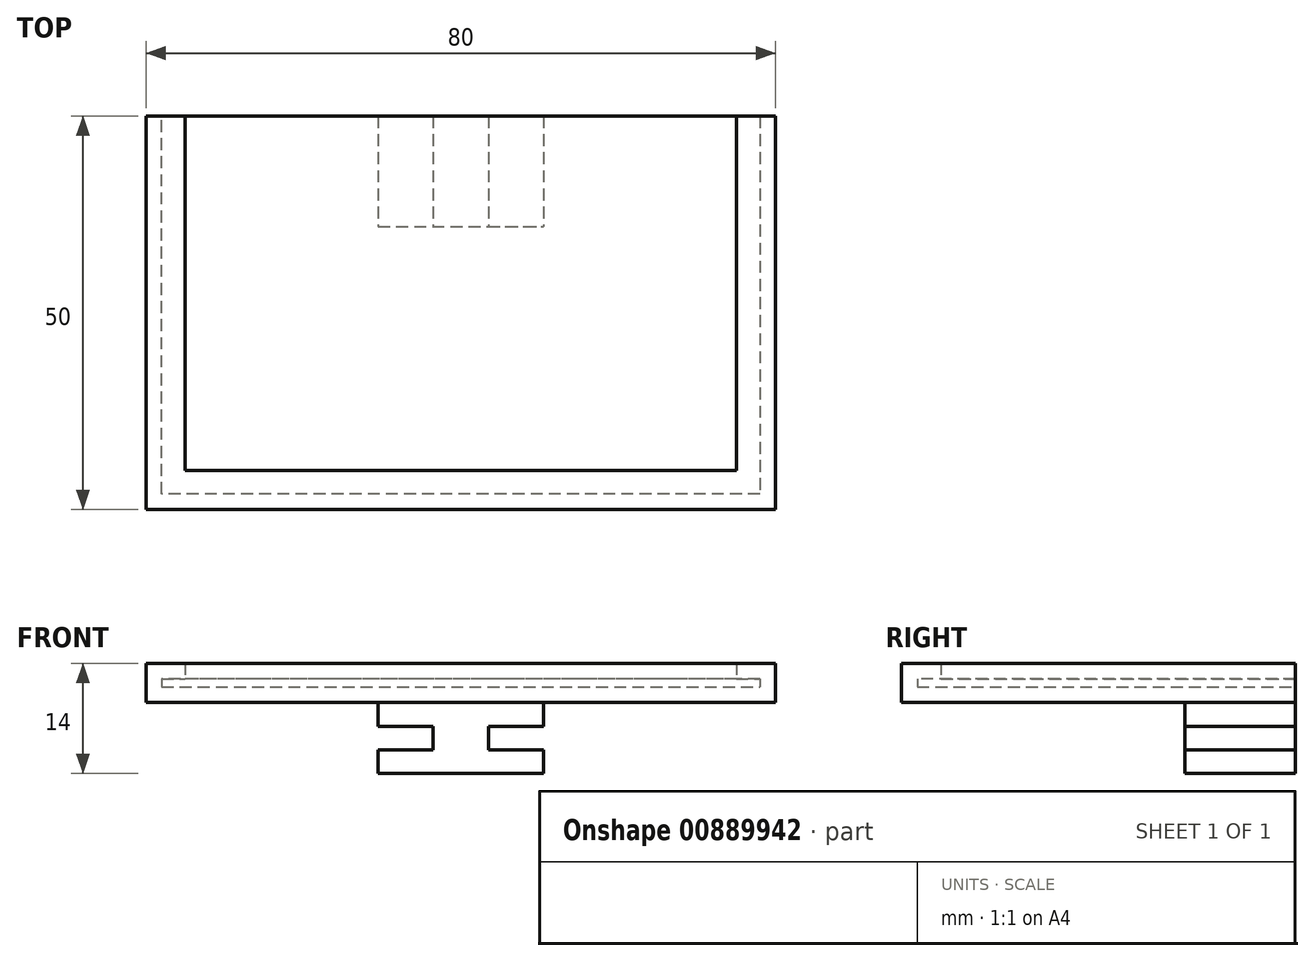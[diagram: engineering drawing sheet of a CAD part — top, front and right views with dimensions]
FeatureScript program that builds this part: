
annotation { "Feature Type Name" : "Feature", "Feature Type Description" : "" }
export const myFeature = defineFeature(function(context is Context, id is Id, definition is map)
    precondition{}
    {
        {
            var Q0;
            Q0=qCreatedBy(makeId("Top.planeOp"),FACE);
            var sketch = newSketch(context, id + "F0", { "sketchPlane" : qUnion([Q0])});
            skLineSegment(sketch, "E0.bottom", {"start": v(-10.5, 7) * mm, "end": v(10.5, 7) * mm});
            skLineSegment(sketch, "E0.top", {"start": v(-10.5, -7) * mm, "end": v(10.5, -7) * mm});
            skLineSegment(sketch, "E0.left", {"start": v(-10.5, 7) * mm, "end": v(-10.5, -7) * mm});
            skLineSegment(sketch, "E0.right", {"start": v(10.5, 7) * mm, "end": v(10.5, -7) * mm});
            skSolve(sketch);
        }
        {
            var Q0;
            Q0=makeQuery(id+"F0.imprint","IMPRINT",FACE,{"disambiguationData":[TD([[makeQuery(id+"F0.imprint","IMPRINT",EDGE,{"derivedFrom":sQuery(id+"F0.wireOp",EDGE,"E0.bottom")}),-1.0]])]});
            extrude(context, id + "F1", {"entities" : qUnion([Q0]), "depth" : 3 * mm, "offsetDistance" : 25 * mm});
        }
        {
            var Q0;
            Q0=makeQuery(id+"F1.opExtrude","CAP_FACE",FACE,{"disambiguationData":[OSD([sQuery(id+"F0.wireOp",EDGE,"E0.bottom"),sQuery(id+"F0.wireOp",EDGE,"E0.top"),sQuery(id+"F0.wireOp",EDGE,"E0.left"),sQuery(id+"F0.wireOp",EDGE,"E0.right")])],"isStart":false});
            var sketch = newSketch(context, id + "F2", { "sketchPlane" : qUnion([Q0])});
            skLineSegment(sketch, "E1.bottom", {"start": v(-3.5, 7) * mm, "end": v(3.5, 7) * mm});
            skLineSegment(sketch, "E1.top", {"start": v(-3.5, -7) * mm, "end": v(3.5, -7) * mm});
            skLineSegment(sketch, "E1.left", {"start": v(-3.5, 7) * mm, "end": v(-3.5, -7) * mm});
            skLineSegment(sketch, "E1.right", {"start": v(3.5, 7) * mm, "end": v(3.5, -7) * mm});
            skSolve(sketch);
        }
        {
            var Q0;
            Q0=makeQuery(id+"F2.imprint","IMPRINT",FACE,{"disambiguationData":[TD([[makeQuery(id+"F2.imprint","IMPRINT",EDGE,{"derivedFrom":sQuery(id+"F2.wireOp",EDGE,"E1.bottom")}),-1.0]])]});
            extrude(context, id + "F3", {"entities" : qUnion([Q0]), "operationType" : NewBodyOperationType.ADD, "depth" : 1.5 * mm, "offsetDistance" : 25 * mm});
        }
        {
            var Q0;
            Q0=makeQuery(id+"F1.opExtrude","SWEPT_BODY",BODY,{"disambiguationData":[OSD([sQuery(id+"F0.wireOp",EDGE,"E0.bottom"),sQuery(id+"F0.wireOp",EDGE,"E0.top"),sQuery(id+"F0.wireOp",EDGE,"E0.left"),sQuery(id+"F0.wireOp",EDGE,"E0.right")])]});
            var Q1;
            Q1=makeQuery(id+"F3.opExtrude","CAP_FACE",FACE,{"disambiguationData":[OSD([sQuery(id+"F2.wireOp",EDGE,"E1.bottom"),sQuery(id+"F2.wireOp",EDGE,"E1.top"),sQuery(id+"F2.wireOp",EDGE,"E1.left"),sQuery(id+"F2.wireOp",EDGE,"E1.right")])],"isStart":false});
            mirror(context, id + "F4", {"operationType" : NewBodyOperationType.ADD, "entities" : qUnion([Q0]), "mirrorPlane" : qUnion([Q1])});
        }
        {
            var Q0;
            Q0=makeQuery(id+"F4.opPattern","COPY",FACE,{"derivedFrom":makeQuery(id+"F1.opExtrude","CAP_FACE",FACE,{"disambiguationData":[OSD([sQuery(id+"F0.wireOp",EDGE,"E0.bottom"),sQuery(id+"F0.wireOp",EDGE,"E0.top"),sQuery(id+"F0.wireOp",EDGE,"E0.left"),sQuery(id+"F0.wireOp",EDGE,"E0.right")])],"isStart":true}),"instanceName":"1"});
            var sketch = newSketch(context, id + "F5", { "sketchPlane" : qUnion([Q0])});
            skLineSegment(sketch, "E2.bottom", {"start": v(-40, 7) * mm, "end": v(40, 7) * mm});
            skLineSegment(sketch, "E2.top", {"start": v(-40, -43) * mm, "end": v(40, -43) * mm});
            skLineSegment(sketch, "E2.left", {"start": v(-40, 7) * mm, "end": v(-40, -43) * mm});
            skLineSegment(sketch, "E2.right", {"start": v(40, 7) * mm, "end": v(40, -43) * mm});
            skSolve(sketch);
        }
        {
            var Q0;
            Q0 = qSketchRegion(id + "F5", true);
            extrude(context, id + "F6", {"entities" : qUnion([Q0]), "operationType" : NewBodyOperationType.ADD, "depth" : 2 * mm, "offsetDistance" : 25 * mm});
        }
        {
            var Q0;
            Q0=makeQuery(id+"F6.opExtrude","CAP_FACE",FACE,{"disambiguationData":[OSD([sQuery(id+"F5.wireOp",EDGE,"E2.bottom"),sQuery(id+"F5.wireOp",EDGE,"E2.top"),sQuery(id+"F5.wireOp",EDGE,"E2.left"),sQuery(id+"F5.wireOp",EDGE,"E2.right")])],"isStart":false});
            var sketch = newSketch(context, id + "F7", { "sketchPlane" : qUnion([Q0])});
            skLineSegment(sketch, "E3", {"start": v(-40, 7) * mm, "end": v(-40, -43) * mm});
            skLineSegment(sketch, "E4", {"start": v(-40, -43) * mm, "end": v(40, -43) * mm});
            skLineSegment(sketch, "E5", {"start": v(40, -43) * mm, "end": v(40, 7) * mm});
            skLineSegment(sketch, "E6", {"start": v(40, 7) * mm, "end": v(38, 7) * mm});
            skLineSegment(sketch, "E7", {"start": v(38, 7) * mm, "end": v(38, -41) * mm});
            skLineSegment(sketch, "E8", {"start": v(38, -41) * mm, "end": v(-38, -41) * mm});
            skLineSegment(sketch, "E9", {"start": v(-38, -41) * mm, "end": v(-38, 7) * mm});
            skLineSegment(sketch, "E10", {"start": v(-38, 7) * mm, "end": v(-40, 7) * mm});
            skSolve(sketch);
        }
        {
            var Q0;
            Q0 = qSketchRegion(id + "F7", true);
            extrude(context, id + "F8", {"entities" : qUnion([Q0]), "operationType" : NewBodyOperationType.ADD, "depth" : 1 * mm, "offsetDistance" : 25 * mm});
        }
        {
            var Q0;
            Q0=makeQuery(id+"F8.opExtrude","CAP_FACE",FACE,{"disambiguationData":[OSD([sQuery(id+"F7.wireOp",EDGE,"E3"),sQuery(id+"F7.wireOp",EDGE,"E4"),sQuery(id+"F7.wireOp",EDGE,"E5"),sQuery(id+"F7.wireOp",EDGE,"E6"),sQuery(id+"F7.wireOp",EDGE,"E7"),sQuery(id+"F7.wireOp",EDGE,"E8"),sQuery(id+"F7.wireOp",EDGE,"E9"),sQuery(id+"F7.wireOp",EDGE,"E10")])],"isStart":false});
            var sketch = newSketch(context, id + "F9", { "sketchPlane" : qUnion([Q0])});
            skLineSegment(sketch, "E11", {"start": v(-40, 7) * mm, "end": v(-40, -43) * mm});
            skLineSegment(sketch, "E12", {"start": v(-40, -43) * mm, "end": v(40, -43) * mm});
            skLineSegment(sketch, "E13", {"start": v(40, -43) * mm, "end": v(40, 7) * mm});
            skLineSegment(sketch, "E14", {"start": v(40, 7) * mm, "end": v(35, 7) * mm});
            skLineSegment(sketch, "E15", {"start": v(35, 7) * mm, "end": v(35, -38) * mm});
            skLineSegment(sketch, "E16", {"start": v(35, -38) * mm, "end": v(-35, -38) * mm});
            skLineSegment(sketch, "E17", {"start": v(-35, -38) * mm, "end": v(-35, 7) * mm});
            skLineSegment(sketch, "E18", {"start": v(-35, 7) * mm, "end": v(-40, 7) * mm});
            skSolve(sketch);
        }
        {
            var Q0;
            Q0 = qSketchRegion(id + "F9", true);
            extrude(context, id + "F10", {"entities" : qUnion([Q0]), "operationType" : NewBodyOperationType.ADD, "depth" : 2 * mm, "offsetDistance" : 25 * mm});
        }
    });
